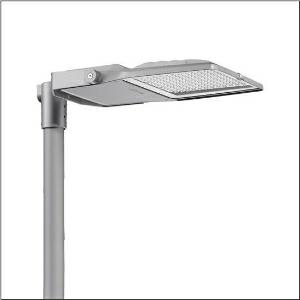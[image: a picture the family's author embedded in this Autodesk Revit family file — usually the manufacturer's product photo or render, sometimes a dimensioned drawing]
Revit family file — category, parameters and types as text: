
# Revit family: floodlight_fl_21_iq_midi___pl61_5xa7782e2c3a_85c4
name_source: partatom
category: Lighting Fixtures
units: mm (PartAtom-declared; Revit-internal decimal feet)

## family parameters
Cut with Voids When Loaded = No
Host = Face
Light Source = No
Part Type = Normal
Room Calculation Point = No
Round Connector Dimension = Use Diameter
Shared = No

## types (1)
- --- (1 x LED, 26360 lm, 208.1 W, 3000K)
    Apparent Load = 208 VA
    CIE Flux Codes = 33 65 98 100 100
    Color Rendering = 70
    Color Temperature = 3000K
    Default Elevation = 1800 mm
    Description = Floodlight FL 21 iQ midi, floodlight, primary light control with lens, of PMMA, primary optical cover: protective disc, of toughened safety glass, transparent, light distribution: PL61, light emission: direct distribution, installation type: surface-mounted, LED, High Power LED, rated luminous flux: 26.360lm, luminous efficacy: 127lm/W, light colour: 730, colour temperature: 3000K, control gear: iQ Street-Remote/DALI, control: optimised constant luminous flux control (CLO 2.0), Desk-Remote (wireless, voltage-free reading and setting of iQ features in the workshop via application-optimized NFC function/RFID function), Smart-Wire, Night-Set, Temp-Guard, Auto-Match, Street-Remote, with terminal, 6-pole, mains connection: 220..240V, AC, 50/60Hz, start of lifetime: 208W, end of service life: 227W, reduction: 90W, luminaire housing, of diecast aluminium, powder-coated, Siteco® metallic grey (DB 702S), corrosivity category C5 mid according to DIN EN ISO 12944, suitable for swimming pools, chlorine-resistant, sealing non-destructively replaceable, please order mast flange separately, mast bracket, of steel, galvanised, powder-coated, Siteco® metallic grey (DB 702S), protection rating (complete): IP66, insulation class (complete): insulation class II (safety insulation), certification: CE, ENEC, VDE, protection symbol: D, impact resistance: IK08, permissible operating ambient temperature: -40..+40°C, permissible operating ambient temperature for outdoor applications: -40..+50°C, standard: DIN EN 12944, LABS conformity tested according to VDMA 24364:2018-05, packaging unit: 1 piece

Light Distribution: PL61
    Height = 76 mm
    Lamp = 1 x LED
    Lamp Light Flux = 26360 lm
    Lamp Power = 208.1 W
    Lamp count = 1
    Length = 657 mm
    Luminous efficacy = 127 lm/W
    Manufacturer = Siteco
    ModVariant = No
    Model = 5XA7782E2C3A
    Number of Poles = 1
    OnlyDefault = Yes
    Power Factor = 1
    Product Name = Floodlight FL 21 iQ midi | PL61
    Product group = floodlight | pylon annexe
    ProductGroupID = 6200
    Protection Class = Protection class II
    Protection Degree = IP 66
    RLX_Detail_Level = 1
    RLX_Emergency_Light_Flux = 0 lm
    RLX_Emergency_Type = 0
    RLX_Emergency_Type_DB = No
    RlxData = <blob elided: 154261 chars, md5=a6523193>
    Socket = socket
    Standby Power = 0 W
    System Light Flux = 26360 lm
    System Power = 208 W
    Type Comments = factory setting: luminous flux: 100 % | dim-lin: 254 | 710 mA
    Type Image = l_1007123.jpg
    URL = http://relux.com
    VarID = @adj_108748
    Voltage = 0 V
    Weight = 0.00 kg
    Width = 442 mm

## geometry (parser evidence)
native form markers: Blend x4, Sweep x13
no freeform markers — native parametric forms only
